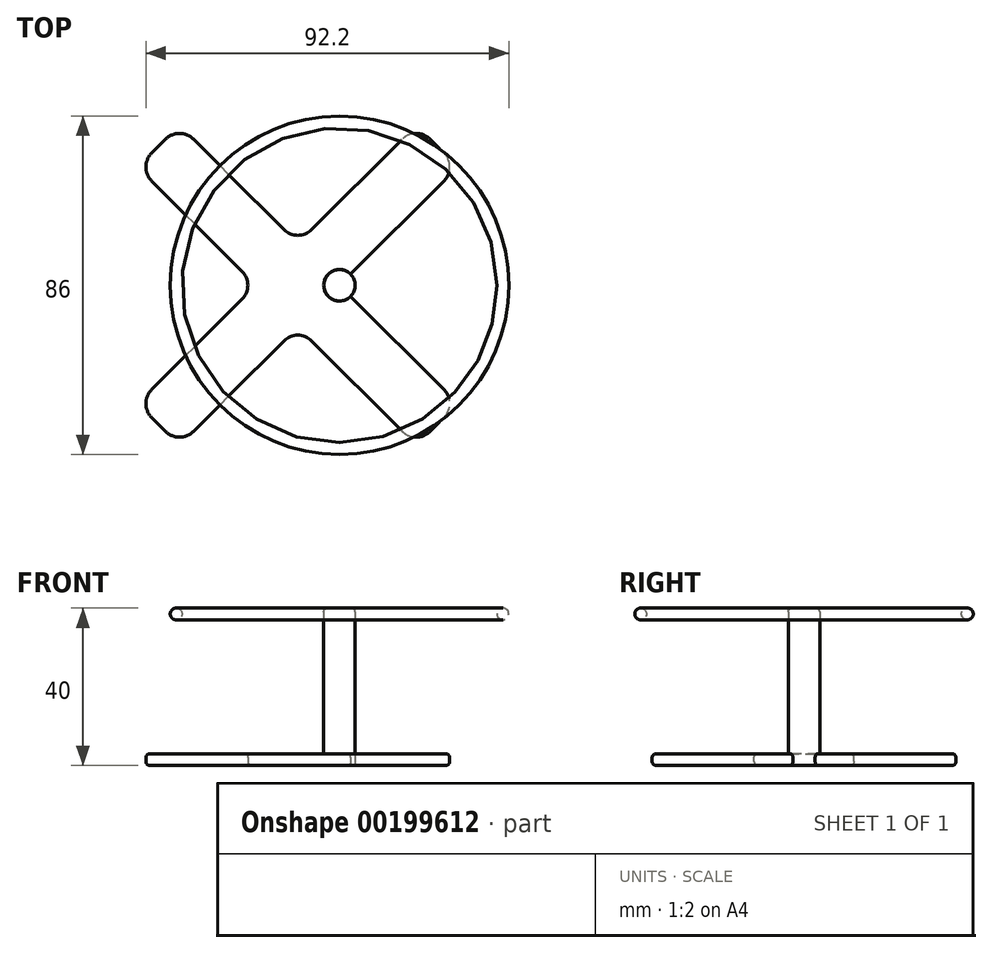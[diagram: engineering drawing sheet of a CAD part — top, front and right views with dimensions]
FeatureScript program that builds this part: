
annotation { "Feature Type Name" : "Feature", "Feature Type Description" : "" }
export const myFeature = defineFeature(function(context is Context, id is Id, definition is map)
    precondition{}
    {
        {
            var Q0;
            Q0=qCreatedBy(makeId("Top.planeOp"),FACE);
            var sketch = newSketch(context, id + "F0", { "sketchPlane" : qUnion([Q0])});
            skLineSegment(sketch, "E0.bottom", {"start": v(50, -7.5) * mm, "end": v(-50, -7.5) * mm});
            skLineSegment(sketch, "E0.top", {"start": v(50, 7.5) * mm, "end": v(-50, 7.5) * mm});
            skLineSegment(sketch, "E0.left", {"start": v(50, -7.5) * mm, "end": v(50, 7.5) * mm});
            skLineSegment(sketch, "E0.right", {"start": v(-50, -7.5) * mm, "end": v(-50, 7.5) * mm});
            skPoint(sketch, "E0.middle", {"position": v(0, 0) * mm});
            skLineSegment(sketch, "E1.bottom", {"start": v(7.5, -50) * mm, "end": v(-7.5, -50) * mm});
            skLineSegment(sketch, "E1.top", {"start": v(7.5, 50) * mm, "end": v(-7.5, 50) * mm});
            skLineSegment(sketch, "E1.left", {"start": v(7.5, -50) * mm, "end": v(7.5, 50) * mm});
            skLineSegment(sketch, "E1.right", {"start": v(-7.5, -50) * mm, "end": v(-7.5, 50) * mm});
            skPoint(sketch, "E2", {"position": v(-7.5, 7.5) * mm});
            skCircle(sketch, "E3", {"center": v(-7.5, 7.5) * mm, "radius": 4 * mm});
            skSolve(sketch);
        }
        {
            var Q0;
            Q0=qCreatedBy(makeId("Front.planeOp"),FACE);
            var sketch = newSketch(context, id + "F1", { "sketchPlane" : qUnion([Q0])});
            skLineSegment(sketch, "E4", {"start": v(0, 0) * mm, "end": v(0, 53.12) * mm});
            skSolve(sketch);
        }
        {
            var Q0;
            {var subQ0=sQuery(id+"F0.wireOp",EDGE,"E0.right");Q0=makeQuery(id+"F0.imprint","IMPRINT",FACE,{"disambiguationData":[TD([[makeQuery(id+"F0.imprint","IMPRINT",EDGE,{"derivedFrom":subQ0}),-1.0]])]});}
            var Q1;
            {var subQ1=sQuery(id+"F0.wireOp",EDGE,"E1.top");Q1=makeQuery(id+"F0.imprint","IMPRINT",FACE,{"disambiguationData":[TD([[makeQuery(id+"F0.imprint","IMPRINT",EDGE,{"derivedFrom":subQ1}),1.0]])]});}
            var Q2;
            {var subQ0=sQuery(id+"F0.wireOp",EDGE,"E1.left");var subQ1=sQuery(id+"F0.wireOp",EDGE,"E0.bottom");var subQ2=makeQuery(id+"F0.imprint","INTERSECT",VERTEX,{"derivedFrom":[subQ1,subQ0]});Q2=makeQuery(id+"F0.imprint","IMPRINT",FACE,{"disambiguationData":[TD([[makeQuery(id+"F0.imprint","IMPRINT",EDGE,{"disambiguationData":[TD([[subQ2,-1.0]])],"derivedFrom":subQ1}),-1.0]])]});}
            var Q3;
            {var subQ0=sQuery(id+"F0.wireOp",EDGE,"E1.left");var subQ1=sQuery(id+"F0.wireOp",EDGE,"E0.bottom");var subQ2=makeQuery(id+"F0.imprint","INTERSECT",VERTEX,{"derivedFrom":[subQ1,subQ0]});Q3=makeQuery(id+"F0.imprint","IMPRINT",FACE,{"disambiguationData":[TD([[makeQuery(id+"F0.imprint","IMPRINT",EDGE,{"disambiguationData":[TD([[subQ2,-1.0]])],"derivedFrom":subQ1}),1.0]])]});}
            var Q4;
            {var subQ0=sQuery(id+"F0.wireOp",EDGE,"IANQtHRf-6u9T-R9gK-CBoC-TykhbRa9lMw2");var subQ1=sQuery(id+"F0.wireOp",EDGE,"E0.bottom");var subQ2=makeQuery(id+"F0.imprint","INTERSECT",VERTEX,{"derivedFrom":[subQ1,subQ0]});Q4=makeQuery(id+"F0.imprint","IMPRINT",FACE,{"disambiguationData":[TD([[makeQuery(id+"F0.imprint","IMPRINT",EDGE,{"disambiguationData":[TD([[subQ2,-1.0]])],"derivedFrom":subQ1}),-1.0]])]});}
            var Q5;
            {var subQ0=sQuery(id+"F0.wireOp",EDGE,"95a81c10-0833-4a51-a1e5-3ae64d37e491.0");var subQ1=sQuery(id+"F0.wireOp",EDGE,"E0.bottom");var subQ2=makeQuery(id+"F0.imprint","INTERSECT",VERTEX,{"derivedFrom":[subQ1,subQ0]});Q5=makeQuery(id+"F0.imprint","IMPRINT",FACE,{"disambiguationData":[TD([[makeQuery(id+"F0.imprint","IMPRINT",EDGE,{"disambiguationData":[TD([[subQ2,-1.0]])],"derivedFrom":subQ1}),-1.0]])]});}
            var Q6;
            {var subQ0=sQuery(id+"F0.wireOp",EDGE,"E0.left");Q6=makeQuery(id+"F0.imprint","IMPRINT",FACE,{"disambiguationData":[TD([[makeQuery(id+"F0.imprint","IMPRINT",EDGE,{"derivedFrom":subQ0}),1.0]])]});}
            var Q7;
            {var subQ0=sQuery(id+"F0.wireOp",EDGE,"95a81c10-0833-4a51-a1e5-3ae64d37e491.0");var subQ1=sQuery(id+"F0.wireOp",EDGE,"E1.left");var subQ2=makeQuery(id+"F0.imprint","INTERSECT",VERTEX,{"derivedFrom":[subQ1,subQ0]});Q7=makeQuery(id+"F0.imprint","IMPRINT",FACE,{"disambiguationData":[TD([[makeQuery(id+"F0.imprint","IMPRINT",EDGE,{"disambiguationData":[TD([[subQ2,-1.0]])],"derivedFrom":subQ1}),1.0]])]});}
            var Q8;
            {var subQ0=sQuery(id+"F0.wireOp",EDGE,"E1.bottom");Q8=makeQuery(id+"F0.imprint","IMPRINT",FACE,{"disambiguationData":[TD([[makeQuery(id+"F0.imprint","IMPRINT",EDGE,{"derivedFrom":subQ0}),-1.0]])]});}
            extrude(context, id + "F2", {"entities" : qUnion([Q0, Q1, Q2, Q3, Q4, Q5, Q6, Q7, Q8]), "depth" : 3 * mm});
        }
        {
            var Q0;
            {var subQ0=sQuery(id+"F0.wireOp",EDGE,"E3");var subQ1=sQuery(id+"F0.wireOp",EDGE,"E0.top");var subQ2=makeQuery(id+"F0.imprint","INTERSECT",VERTEX,{"disambiguationData":[OD(1.0)],"derivedFrom":[subQ1,subQ0]});Q0=makeQuery(id+"F0.imprint","IMPRINT",FACE,{"disambiguationData":[TD([[makeQuery(id+"F0.imprint","IMPRINT",EDGE,{"disambiguationData":[TD([[subQ2,-1.0]])],"derivedFrom":subQ1}),-1.0]])]});}
            var Q1;
            {var subQ0=sQuery(id+"F0.wireOp",EDGE,"E3");var subQ1=sQuery(id+"F0.wireOp",EDGE,"E0.top");var subQ2=makeQuery(id+"F0.imprint","INTERSECT",VERTEX,{"disambiguationData":[OD(0.0)],"derivedFrom":[subQ1,subQ0]});Q1=makeQuery(id+"F0.imprint","IMPRINT",FACE,{"disambiguationData":[TD([[makeQuery(id+"F0.imprint","IMPRINT",EDGE,{"disambiguationData":[TD([[subQ2,1.0]])],"derivedFrom":subQ1}),1.0]])]});}
            var Q2;
            {var subQ0=sQuery(id+"F0.wireOp",EDGE,"E3");var subQ1=sQuery(id+"F0.wireOp",EDGE,"E0.top");var subQ2=makeQuery(id+"F0.imprint","INTERSECT",VERTEX,{"disambiguationData":[OD(1.0)],"derivedFrom":[subQ1,subQ0]});Q2=makeQuery(id+"F0.imprint","IMPRINT",FACE,{"disambiguationData":[TD([[makeQuery(id+"F0.imprint","IMPRINT",EDGE,{"disambiguationData":[TD([[subQ2,-1.0]])],"derivedFrom":subQ1}),1.0]])]});}
            var Q3;
            {var subQ0=sQuery(id+"F0.wireOp",EDGE,"E3");var subQ1=sQuery(id+"F0.wireOp",EDGE,"E0.top");var subQ2=makeQuery(id+"F0.imprint","INTERSECT",VERTEX,{"disambiguationData":[OD(0.0)],"derivedFrom":[subQ1,subQ0]});Q3=makeQuery(id+"F0.imprint","IMPRINT",FACE,{"disambiguationData":[TD([[makeQuery(id+"F0.imprint","IMPRINT",EDGE,{"disambiguationData":[TD([[subQ2,1.0]])],"derivedFrom":subQ1}),-1.0]])]});}
            extrude(context, id + "F3", {"entities" : qUnion([Q0, Q1, Q2, Q3]), "operationType" : NewBodyOperationType.ADD, "depth" : 40 * mm});
        }
        {
            var Q0;
            Q0=makeQuery(id+"F3.opExtrude","CAP_FACE",FACE,{"disambiguationData":[OSD([sQuery(id+"F0.wireOp",EDGE,"E3")])],"isStart":false});
            var sketch = newSketch(context, id + "F4", { "sketchPlane" : qUnion([Q0])});
            skCircle(sketch, "E5", {"center": v(-7.5, 7.5) * mm, "radius": 40 * mm});
            skCircle(sketch, "E6.0", {"center": v(-7.5, 7.5) * mm, "radius": 43 * mm});
            skSolve(sketch);
        }
        {
            var Q0;
            Q0=makeQuery(id+"F4.imprint","IMPRINT",FACE,{"disambiguationData":[TD([[makeQuery(id+"F4.imprint","IMPRINT",EDGE,{"derivedFrom":sQuery(id+"F4.wireOp",EDGE,"E5")}),-1.0]])]});
            extrude(context, id + "F5", {"entities" : qUnion([Q0]), "oppositeDirection" : true, "depth" : 3 * mm});
        }
        {
            var Q0;
            Q0=makeQuery(id+"F2.opExtrude","SWEPT_EDGE",EDGE,{"disambiguationData":[OSD([sQuery(id+"F0.wireOp",EDGE,"E0.bottom"),sQuery(id+"F0.wireOp",EDGE,"E1.left")])]});
            var Q1;
            Q1=makeQuery(id+"F2.opExtrude","SWEPT_EDGE",EDGE,{"disambiguationData":[OSD([sQuery(id+"F0.wireOp",EDGE,"E0.bottom"),sQuery(id+"F0.wireOp",EDGE,"E0.left")])]});
            var Q2;
            Q2=makeQuery(id+"F2.opExtrude","SWEPT_EDGE",EDGE,{"disambiguationData":[OSD([sQuery(id+"F0.wireOp",EDGE,"E1.bottom"),sQuery(id+"F0.wireOp",EDGE,"E1.left")])]});
            var Q3;
            Q3=makeQuery(id+"F2.opExtrude","SWEPT_EDGE",EDGE,{"disambiguationData":[OSD([sQuery(id+"F0.wireOp",EDGE,"E1.bottom"),sQuery(id+"F0.wireOp",EDGE,"E1.right")])]});
            var Q4;
            Q4=makeQuery(id+"F2.opExtrude","SWEPT_EDGE",EDGE,{"disambiguationData":[OSD([sQuery(id+"F0.wireOp",EDGE,"E0.bottom"),sQuery(id+"F0.wireOp",EDGE,"E1.right")])]});
            var Q5;
            Q5=makeQuery(id+"F2.opExtrude","SWEPT_EDGE",EDGE,{"disambiguationData":[OSD([sQuery(id+"F0.wireOp",EDGE,"E0.bottom"),sQuery(id+"F0.wireOp",EDGE,"E0.right")])]});
            var Q6;
            Q6=makeQuery(id+"F2.opExtrude","SWEPT_EDGE",EDGE,{"disambiguationData":[OSD([sQuery(id+"F0.wireOp",EDGE,"E0.top"),sQuery(id+"F0.wireOp",EDGE,"E0.right")])]});
            var Q7;
            Q7=makeQuery(id+"F2.opExtrude","SWEPT_EDGE",EDGE,{"disambiguationData":[OSD([sQuery(id+"F0.wireOp",EDGE,"E0.top"),sQuery(id+"F0.wireOp",EDGE,"E3")])]});
            var Q8;
            Q8=makeQuery(id+"F2.opExtrude","SWEPT_EDGE",EDGE,{"disambiguationData":[OSD([sQuery(id+"F0.wireOp",EDGE,"E1.right"),sQuery(id+"F0.wireOp",EDGE,"E3")])]});
            var Q9;
            Q9=makeQuery(id+"F2.opExtrude","SWEPT_EDGE",EDGE,{"disambiguationData":[OSD([sQuery(id+"F0.wireOp",EDGE,"E1.top"),sQuery(id+"F0.wireOp",EDGE,"E1.right")])]});
            var Q10;
            Q10=makeQuery(id+"F2.opExtrude","SWEPT_EDGE",EDGE,{"disambiguationData":[OSD([sQuery(id+"F0.wireOp",EDGE,"E1.top"),sQuery(id+"F0.wireOp",EDGE,"E1.left")])]});
            var Q11;
            Q11=makeQuery(id+"F2.opExtrude","SWEPT_EDGE",EDGE,{"disambiguationData":[OSD([sQuery(id+"F0.wireOp",EDGE,"E0.top"),sQuery(id+"F0.wireOp",EDGE,"E1.left")])]});
            var Q12;
            Q12=makeQuery(id+"F2.opExtrude","SWEPT_EDGE",EDGE,{"disambiguationData":[OSD([sQuery(id+"F0.wireOp",EDGE,"E0.top"),sQuery(id+"F0.wireOp",EDGE,"E0.left")])]});
            fillet(context, id + "F6", {"entities" : qUnion([Q0, Q1, Q2, Q3, Q4, Q5, Q6, Q7, Q8, Q9, Q10, Q11, Q12]), "radius" : 5 * mm, "tangentPropagation" : true, "allowEdgeOverflow" : false});
        }
        {
            var Q0;
            {var subQ0=sQuery(id+"F0.wireOp",EDGE,"E0.top");Q0=makeQuery(id+"F2.opExtrude","CAP_EDGE",EDGE,{"disambiguationData":[OSD([subQ0]),TDD([makeQuery(id+"F0.imprint","IMPRINT",EDGE,{"disambiguationData":[TD([[makeQuery(id+"F0.imprint","INTERSECT",VERTEX,{"derivedFrom":[subQ0,sQuery(id+"F0.wireOp",EDGE,"E0.left")]}),-1.0]])],"derivedFrom":subQ0})])],"isStart":false});}
            var Q1;
            {var subQ0=sQuery(id+"F0.wireOp",EDGE,"E0.top");Q1=makeQuery(id+"F2.opExtrude","CAP_EDGE",EDGE,{"disambiguationData":[OSD([subQ0]),TDD([makeQuery(id+"F0.imprint","IMPRINT",EDGE,{"disambiguationData":[TD([[makeQuery(id+"F0.imprint","INTERSECT",VERTEX,{"derivedFrom":[subQ0,sQuery(id+"F0.wireOp",EDGE,"E0.left")]}),-1.0]])],"derivedFrom":subQ0})])],"isStart":true});}
            var Q2;
            Q2=makeQuery(id+"F2.opExtrude","CAP_EDGE",EDGE,{"disambiguationData":[OSD([sQuery(id+"F0.wireOp",EDGE,"E3")])],"isStart":false});
            var Q3;
            Q3=makeQuery(id+"F3.opExtrude","CAP_EDGE",EDGE,{"disambiguationData":[OSD([sQuery(id+"F0.wireOp",EDGE,"E3")])],"isStart":false});
            fillet(context, id + "F7", {"entities" : qUnion([Q0, Q1, Q2, Q3]), "radius" : 1 * mm, "tangentPropagation" : true, "allowEdgeOverflow" : false});
        }
        {
            var Q0;
            Q0=makeQuery(id+"F2.opExtrude","SWEPT_BODY",BODY,{"disambiguationData":[OSD([sQuery(id+"F0.wireOp",EDGE,"E0.bottom"),sQuery(id+"F0.wireOp",EDGE,"E0.top"),sQuery(id+"F0.wireOp",EDGE,"E0.left"),sQuery(id+"F0.wireOp",EDGE,"E0.right"),sQuery(id+"F0.wireOp",EDGE,"E1.bottom"),sQuery(id+"F0.wireOp",EDGE,"E1.top"),sQuery(id+"F0.wireOp",EDGE,"E1.left"),sQuery(id+"F0.wireOp",EDGE,"E1.right")])]});
            var Q1;
            Q1=makeQuery(id+"F5.opExtrude","SWEPT_BODY",BODY,{"disambiguationData":[OSD([sQuery(id+"F4.wireOp",EDGE,"E5"),sQuery(id+"F4.wireOp",EDGE,"E6.0")])]});
            var Q2;
            Q2=sQuery(id+"F1.wireOp",EDGE,"E4");
            transform(context, id + "F8", {"entities" : qUnion([Q0, Q1]), "transformType" : TransformType.ROTATION, "transformAxis" : qUnion([Q2]), "angle" : 225 * degree, "makeCopy" : false});
        }
        {
            var Q0;
            Q0=makeQuery(id+"F5.opExtrude","CAP_EDGE",EDGE,{"disambiguationData":[OSD([sQuery(id+"F4.wireOp",EDGE,"E5")])],"isStart":true});
            var Q1;
            Q1=makeQuery(id+"F5.opExtrude","CAP_EDGE",EDGE,{"disambiguationData":[OSD([sQuery(id+"F4.wireOp",EDGE,"E6.0")])],"isStart":true});
            var Q2;
            Q2=makeQuery(id+"F5.opExtrude","CAP_EDGE",EDGE,{"disambiguationData":[OSD([sQuery(id+"F4.wireOp",EDGE,"E5")])],"isStart":false});
            var Q3;
            Q3=makeQuery(id+"F5.opExtrude","CAP_EDGE",EDGE,{"disambiguationData":[OSD([sQuery(id+"F4.wireOp",EDGE,"E6.0")])],"isStart":false});
            fillet(context, id + "F9", {"entities" : qUnion([Q0, Q1, Q2, Q3]), "radius" : 1.5 * mm, "tangentPropagation" : true, "allowEdgeOverflow" : false});
        }
    });
